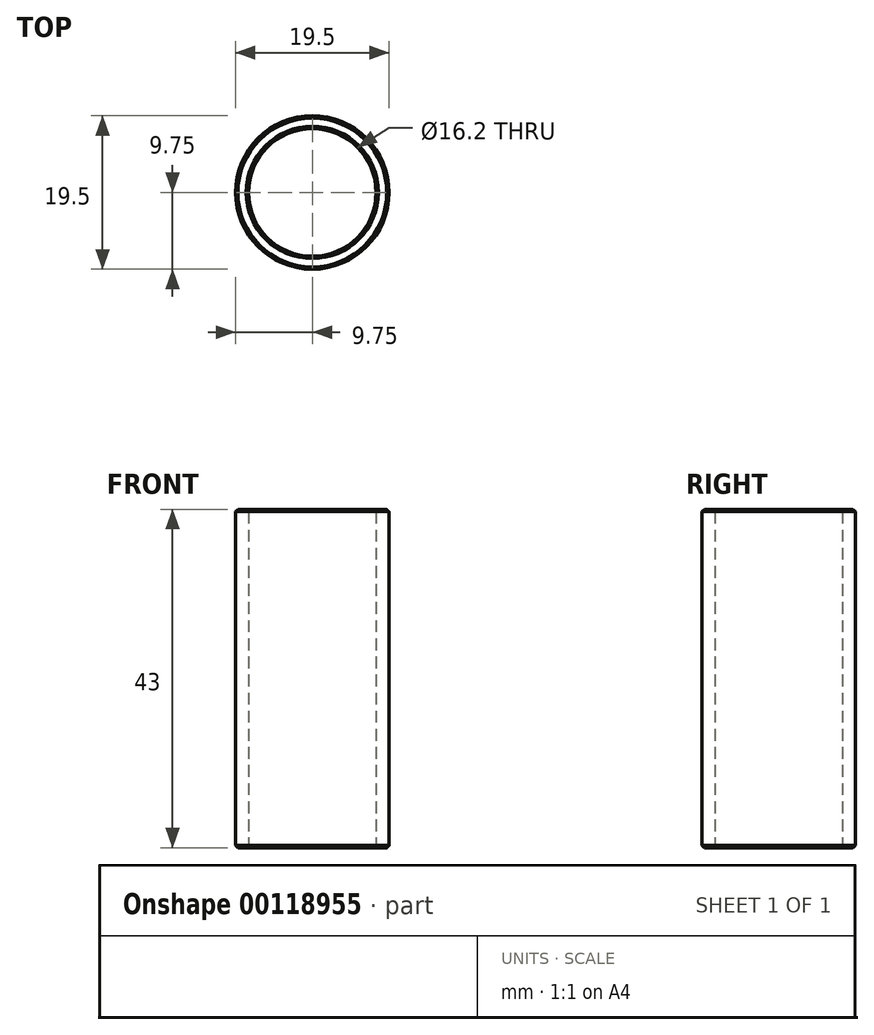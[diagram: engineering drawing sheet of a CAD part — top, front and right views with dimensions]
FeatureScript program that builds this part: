
annotation { "Feature Type Name" : "Feature", "Feature Type Description" : "" }
export const myFeature = defineFeature(function(context is Context, id is Id, definition is map)
    precondition{}
    {
        {
            var Q0;
            Q0=qCreatedBy(makeId("Top.planeOp"),FACE);
            var sketch = newSketch(context, id + "F0", { "sketchPlane" : qUnion([Q0])});
            skCircle(sketch, "E0", {"center": v(0, 0) * mm, "radius": 9.75 * mm});
            skCircle(sketch, "E1", {"center": v(0, 0) * mm, "radius": 8.1 * mm});
            skSolve(sketch);
        }
        {
            var Q0;
            Q0 = qSketchRegion(id + "F0", true);
            extrude(context, id + "F1", {"entities" : qUnion([Q0]), "depth" : 43 * mm, "offsetDistance" : 25 * mm});
        }
        {
            var Q0;
            Q0=makeQuery(id+"F1.opExtrude","SWEPT_FACE",FACE,{"disambiguationData":[OSD([sQuery(id+"F0.wireOp",EDGE,"E0")])]});
            var Q1;
            Q1=makeQuery(id+"F1.opExtrude","SWEPT_FACE",FACE,{"disambiguationData":[OSD([sQuery(id+"F0.wireOp",EDGE,"E1")])]});
            chamfer(context, id + "F2", {"entities" : qUnion([Q0, Q1]), "width" : 0.3 * mm, "tangentPropagation" : true});
        }
    });
